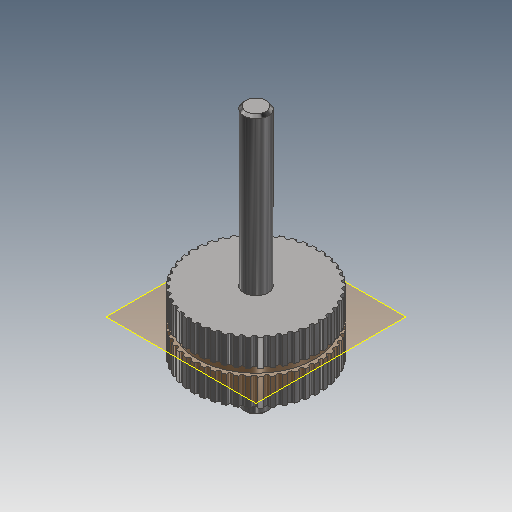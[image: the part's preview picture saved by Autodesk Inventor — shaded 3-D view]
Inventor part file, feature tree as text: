
AUTODESK INVENTOR PART (.ipt)
format: ipt  version: 2020.2 (Build 242310000, 310)  size: 363,008 bytes
history: native  units: mm
features: extrude x7, sketch x7, plane x3, chamfer x1, pattern_circular x1, projected_geometry x1
ambient origin geometry x8: Origin, YZ Plane, XZ Plane, XY Plane, X Axis, Y Axis, Z Axis, Center Point
bodies: Solid7 (feature_tree), Solid8 (feature_tree), Solid9 (feature_tree)
feature tree (20):
  extrude  "Extrusion7"  Depth=2.0mm TaperAngle=0.0deg
  chamfer  "Chamfer1"  Distance=0.5mm Angle=45.0deg
  extrude  "Extrusion8"  Depth=18.0mm TaperAngle=0.0deg
  plane  "Work Plane6"
  extrude  "Extrusion9"  Depth=5.5mm TaperAngle=0.0deg
  plane  "Work Plane7"
  extrude  "Extrusion10"  Depth=5.5mm TaperAngle=0.0deg
  extrude  "Extrusion11"  Depth=27.0mm TaperAngle=0.0deg
  pattern_circular  "Circular Pattern1"  Count=45 Angle=360.0deg
  extrude  "Extrusion12"  Depth=34.0mm TaperAngle=0.0deg
  plane  "Work Plane8"
  extrude  "Extrusion13"  Depth=0.75mm
  sketch  "Sketch11"  dims[d82=5.0mm d83=53.0mm d84=0.0mm d85=0.5mm d86=2.0mm d87=45.0deg]
  sketch  "Sketch12"  dims[d88=4.5mm d89=18.0mm d90=0.0mm]
  sketch  "Sketch13"  dims[d91=-8.75mm d92=5.5mm d93=0.0mm]
  sketch  "Sketch14"  dims[d94=1.5mm d95=5.5mm d96=0.0mm]
  projected_geometry  "Projected Loop3"
  sketch  "Sketch15"  dims[d97=1.0mm d98=27.0mm d99=0.0mm d100=450.0mm d101=360.0deg]
  sketch  "Sketch16"  dims[d103=24.0mm d104=34.0mm d105=0.0mm]
  sketch  "Sketch17"  dims[d106=-5.0mm d107=4.0mm d108=0.75mm d109=0.0mm d110=25.8mm]
